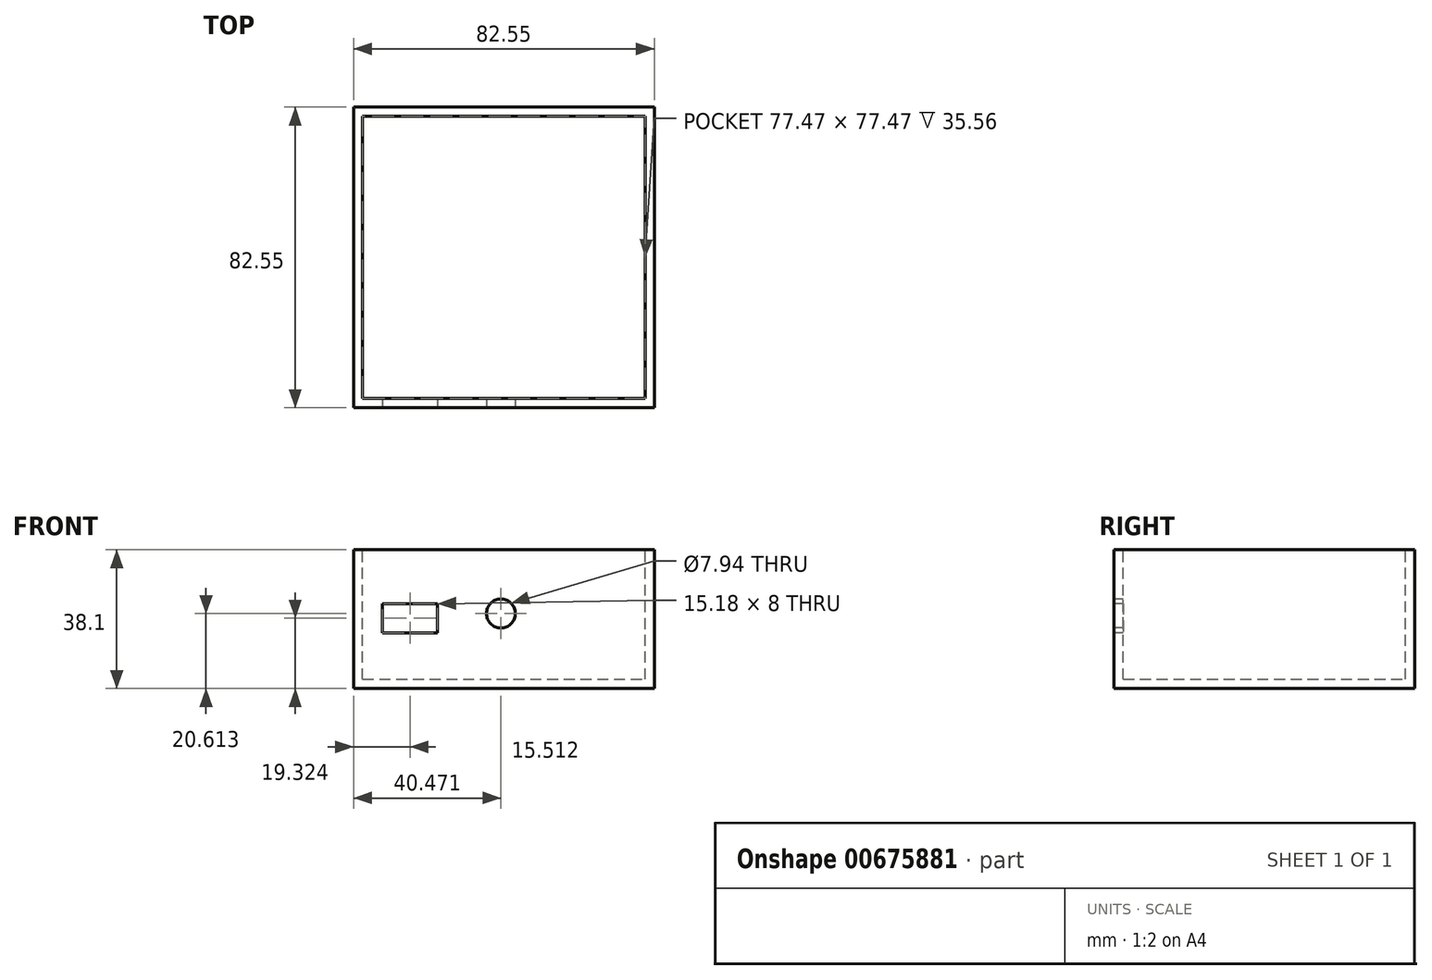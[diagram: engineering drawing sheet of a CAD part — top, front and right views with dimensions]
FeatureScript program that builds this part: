
annotation { "Feature Type Name" : "Feature", "Feature Type Description" : "" }
export const myFeature = defineFeature(function(context is Context, id is Id, definition is map)
    precondition{}
    {
        {
            var Q0;
            Q0=qCreatedBy(makeId("Front.planeOp"),FACE);
            var sketch = newSketch(context, id + "F0", { "sketchPlane" : qUnion([Q0])});
            skLineSegment(sketch, "E0.bottom", {"start": v(0, 0) * mm, "end": v(82.55, 0) * mm});
            skLineSegment(sketch, "E0.top", {"start": v(0, 38.1) * mm, "end": v(82.55, 38.1) * mm});
            skLineSegment(sketch, "E0.left", {"start": v(0, 0) * mm, "end": v(0, 38.1) * mm});
            skLineSegment(sketch, "E0.right", {"start": v(82.55, 0) * mm, "end": v(82.55, 38.1) * mm});
            skSolve(sketch);
        }
        {
            var Q0;
            Q0=makeQuery(id+"F0.imprint","IMPRINT",FACE,{"disambiguationData":[TD([[makeQuery(id+"F0.imprint","IMPRINT",EDGE,{"derivedFrom":sQuery(id+"F0.wireOp",EDGE,"E0.bottom")}),1.0]])]});
            extrude(context, id + "F1", {"entities" : qUnion([Q0]), "depth" : 82.55 * mm, "offsetDistance" : 25.4 * mm});
        }
        {
            var Q0;
            Q0=makeQuery(id+"F1.opExtrude","CAP_FACE",FACE,{"disambiguationData":[OSD([sQuery(id+"F0.wireOp",EDGE,"E0.bottom"),sQuery(id+"F0.wireOp",EDGE,"E0.top"),sQuery(id+"F0.wireOp",EDGE,"E0.left"),sQuery(id+"F0.wireOp",EDGE,"E0.right")])],"isStart":false});
            var sketch = newSketch(context, id + "F2", { "sketchPlane" : qUnion([Q0])});
            skSolve(sketch);
        }
        {
            var Q0;
            Q0=makeQuery(id+"F1.opExtrude","SWEPT_FACE",FACE,{"disambiguationData":[OSD([sQuery(id+"F0.wireOp",EDGE,"E0.top")])]});
            shell(context, id + "F3", {"entities" : qUnion([Q0]), "thickness" : 2.54 * mm});
        }
        {
            var Q0;
            Q0=makeQuery(id+"F2.imprint","IMPRINT",FACE,{"disambiguationData":[TD([[makeQuery(id+"F2.imprint","IMPRINT",EDGE,{"derivedFrom":makeQuery(id+"F1.opExtrude","CAP_EDGE",EDGE,{"disambiguationData":[OSD([sQuery(id+"F0.wireOp",EDGE,"E0.bottom")])],"isStart":false})}),1.0]])]});
            var sketch = newSketch(context, id + "F4", { "sketchPlane" : qUnion([Q0])});
            skPoint(sketch, "E1", {"position": v(40.47, 20.61) * mm});
            skSolve(sketch);
        }
        {
            var Q0;
            Q0=sQuery(id+"F4.wireOp",VERTEX,"E1");
            var Q1;
            Q1=makeQuery(id+"F1.opExtrude","SWEPT_BODY",BODY,{"disambiguationData":[OSD([sQuery(id+"F0.wireOp",EDGE,"E0.bottom"),sQuery(id+"F0.wireOp",EDGE,"E0.top"),sQuery(id+"F0.wireOp",EDGE,"E0.left"),sQuery(id+"F0.wireOp",EDGE,"E0.right")])]});
            hole(context, id + "F5", {"style" : HoleStyle.SIMPLE, "endStyle" : HoleEndStyle.BLIND, "holeDiameter" : 7.94 * mm, "majorDiameter" : 6.35 * mm, "holeDepth" : 12.7 * mm, "isTappedThrough" : true, "tappedDepth" : 12.7 * mm, "tapClearance" : 3, "startFromSketch" : true, "locations" : qUnion([Q0]), "scope" : qUnion([Q1])});
        }
        {
            var Q0;
            Q0=makeQuery(id+"F2.imprint","IMPRINT",FACE,{"disambiguationData":[TD([[makeQuery(id+"F2.imprint","IMPRINT",EDGE,{"derivedFrom":makeQuery(id+"F1.opExtrude","CAP_EDGE",EDGE,{"disambiguationData":[OSD([sQuery(id+"F0.wireOp",EDGE,"E0.bottom")])],"isStart":false})}),1.0]])]});
            var sketch = newSketch(context, id + "F6", { "sketchPlane" : qUnion([Q0])});
            skLineSegment(sketch, "E2.bottom", {"start": v(23.1, 15.32) * mm, "end": v(7.92, 15.32) * mm});
            skLineSegment(sketch, "E2.top", {"start": v(23.1, 23.33) * mm, "end": v(7.92, 23.33) * mm});
            skLineSegment(sketch, "E2.left", {"start": v(23.1, 15.32) * mm, "end": v(23.1, 23.33) * mm});
            skLineSegment(sketch, "E2.right", {"start": v(7.92, 15.32) * mm, "end": v(7.92, 23.33) * mm});
            skPoint(sketch, "E2.middle", {"position": v(15.51, 19.32) * mm});
            skSolve(sketch);
        }
        {
            var Q0;
            Q0=makeQuery(id+"F6.imprint","IMPRINT",FACE,{"disambiguationData":[TD([[makeQuery(id+"F6.imprint","IMPRINT",EDGE,{"derivedFrom":sQuery(id+"F6.wireOp",EDGE,"E2.bottom")}),-1.0]])]});
            extrude(context, id + "F7", {"entities" : qUnion([Q0]), "operationType" : NewBodyOperationType.REMOVE, "endBound" : BoundingType.UP_TO_NEXT, "oppositeDirection" : true, "depth" : 25.4 * mm, "offsetDistance" : 25.4 * mm});
        }
    });
